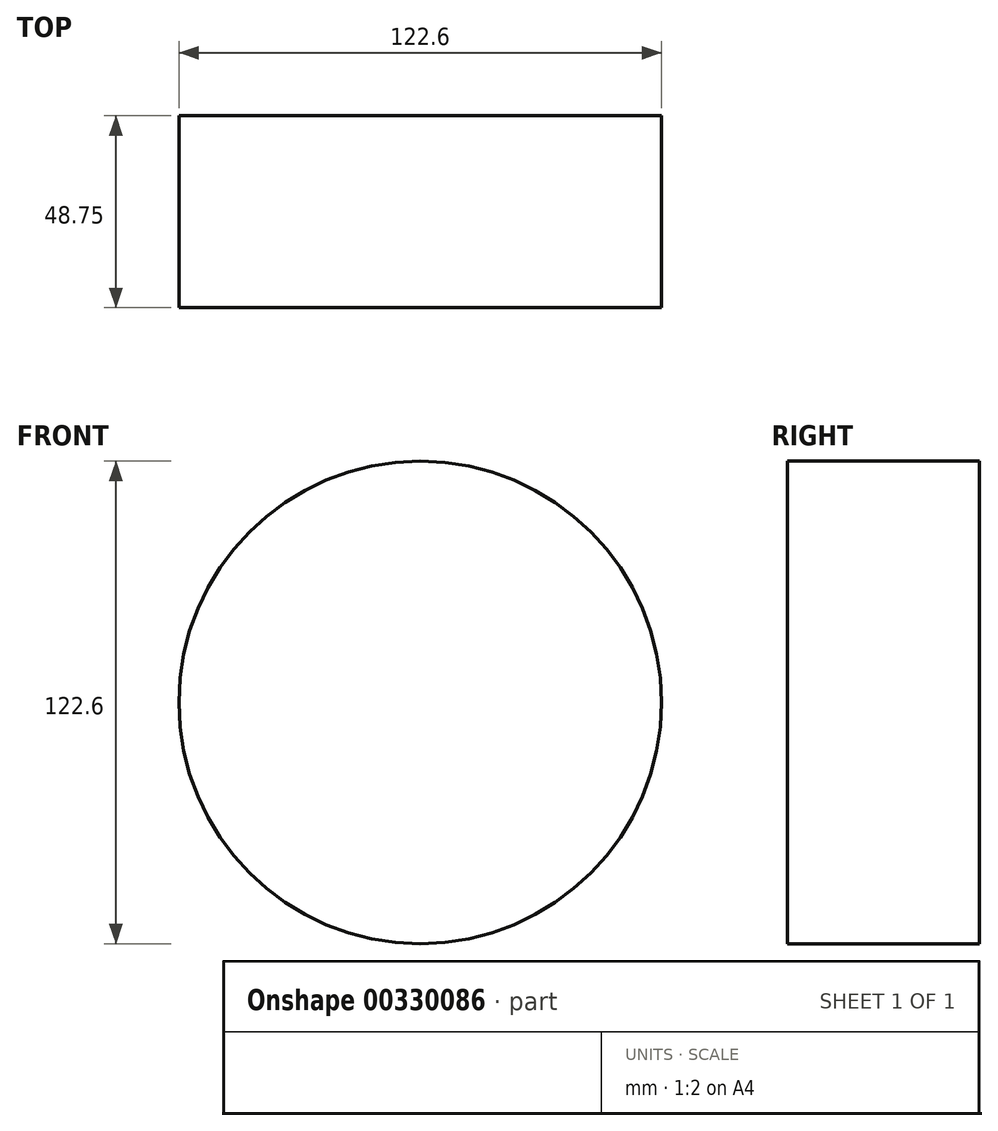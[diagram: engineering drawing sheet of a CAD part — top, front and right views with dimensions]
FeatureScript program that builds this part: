
annotation { "Feature Type Name" : "Feature", "Feature Type Description" : "" }
export const myFeature = defineFeature(function(context is Context, id is Id, definition is map)
    precondition{}
    {
        {
            var Q0;
            Q0=qCreatedBy(makeId("Front.planeOp"),FACE);
            var sketch = newSketch(context, id + "F0", { "sketchPlane" : qUnion([Q0])});
            skCircle(sketch, "E0", {"center": v(1.28, 2.03) * mm, "radius": 61.3 * mm});
            skSolve(sketch);
        }
        {
            var Q0;
            Q0 = qSketchRegion(id + "F0", true);
            extrude(context, id + "F1", {"entities" : qUnion([Q0]), "depth" : 48.75 * mm});
        }
    });
